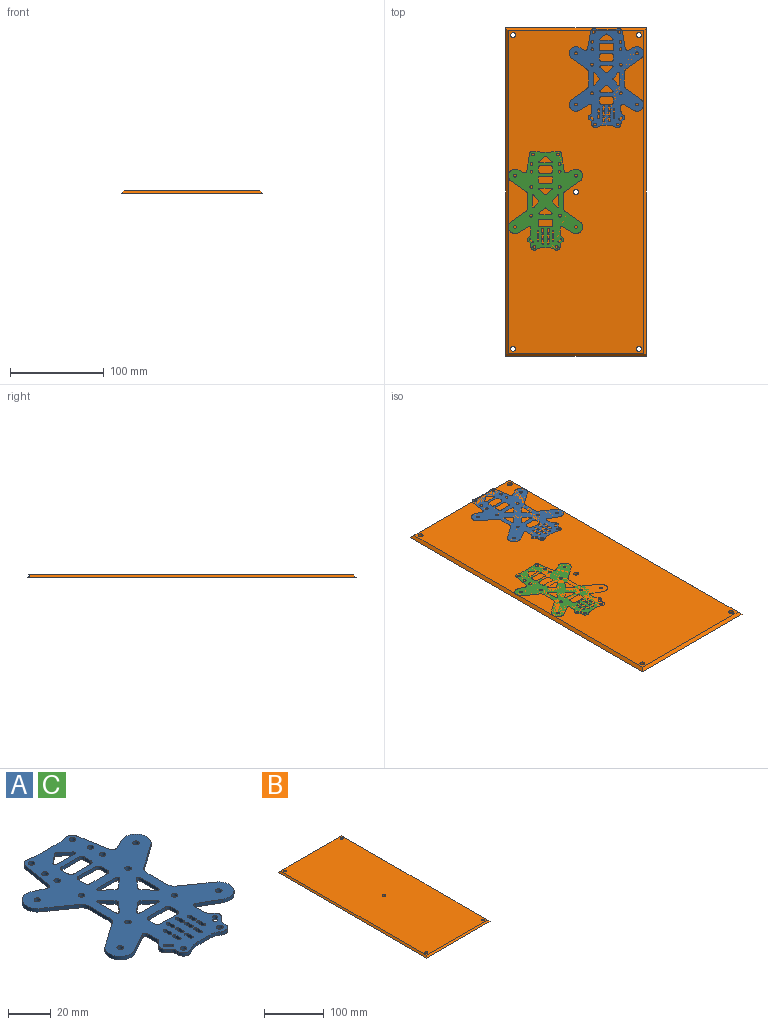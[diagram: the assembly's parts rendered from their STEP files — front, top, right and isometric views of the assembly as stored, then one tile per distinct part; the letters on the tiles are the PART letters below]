
ASSEMBLY  parts=3 mates=2
PART A: 170 faces, bbox 79.1x105.5x2 mm
  f0: plane 2.12x2.12mm, normal (0.71,0.71,0), area 6mm2, adj f1,f134,f168,f169
  f1: cylinder r=1mm len=2mm, axis (0,0,-1), area 6.3mm2, adj f0,f2,f168,f169
  f2: plane 2.12x2.12mm, normal (-0.71,-0.71,0), area 6mm2, adj f1,f134,f168,f169
  f3: cylinder r=1mm len=2mm, axis (0,0,-1), area 6.3mm2, adj f4,f135,f168,f169
  f4: plane 3x2mm, normal (1,0,0), area 6mm2, adj f3,f5,f168,f169
  f5: cylinder r=1mm len=2mm, axis (0,0,-1), area 6.3mm2, adj f4,f135,f168,f169
  f6: plane 3x2mm, normal (1,0,0), area 6mm2, adj f7,f136,f168,f169
  f7: cylinder r=1mm len=2mm, axis (0,0,-1), area 6.3mm2, adj f6,f8,f168,f169
  f8: plane 3x2mm, normal (-1,0,0), area 6mm2, adj f7,f136,f168,f169
  f9: plane 3x2mm, normal (1,0,0), area 6mm2, adj f10,f137,f168,f169
  f10: cylinder r=1mm len=2mm, axis (0,0,-1), area 6.3mm2, adj f9,f11,f168,f169
  f11: plane 3x2mm, normal (-1,0,0), area 6mm2, adj f10,f137,f168,f169
  f12: plane 3x2mm, normal (1,0,0), area 6mm2, adj f13,f138,f168,f169
  f13: cylinder r=1mm len=2mm, axis (0,0,-1), area 6.3mm2, adj f12,f14,f168,f169
  f14: plane 3x2mm, normal (-1,0,0), area 6mm2, adj f13,f138,f168,f169
  f15: plane 3x2mm, normal (1,0,0), area 6mm2, adj f16,f139,f168,f169
  f16: cylinder r=1mm len=2mm, axis (0,0,-1), area 6.3mm2, adj f15,f17,f168,f169
  f17: plane 3x2mm, normal (-1,0,0), area 6mm2, adj f16,f139,f168,f169
  f18: cylinder r=3.5mm len=5.53mm, axis (0,0,-1), area 15.3mm2, adj f19,f140,f168,f169
  f19: plane 2x1.24mm, normal (1,0,0), area 2.5mm2, adj f18,f20,f168,f169
  f20: cylinder r=3mm len=2.12mm, axis (0,0,-1), area 4.7mm2, adj f19,f21,f168,f169
  f21: plane 2.12x2.12mm, normal (0.71,-0.71,0), area 6mm2, adj f20,f22,f168,f169
  f22: cylinder r=3mm len=4.24mm, axis (0,0,-1), area 9.4mm2, adj f21,f23,f168,f169
  f23: plane 2.41x2.41mm, normal (0.71,0.71,0), area 6.8mm2, adj f22,f24,f168,f169
  f24: cylinder r=2mm len=2mm, axis (0,0,-1), area 3.1mm2, adj f23,f25,f168,f169
  f25: plane 6.65x2mm, normal (1,0,0), area 13.3mm2, adj f24,f26,f168,f169
  f26: cylinder r=1.5mm len=2.25mm, axis (0,0,-1), area 6.3mm2, adj f25,f27,f168,f169
  f27: plane 11.16x6.44mm, normal (-0.5,-0.87,0), area 25.8mm2, adj f26,f28,f168,f169
  f28: cylinder r=7.09mm len=12.9mm, axis (0,0,-1), area 43.3mm2, adj f27,f29,f168,f169
  f29: plane 15.33x10.73mm, normal (0.57,0.82,0), area 37.4mm2, adj f28,f30,f168,f169
  f30: cylinder r=5.14mm len=4.21mm, axis (0,0,-1), area 9.9mm2, adj f29,f31,f168,f169
  f31: plane 13.09x2mm, normal (1,0,0), area 26.2mm2, adj f30,f32,f168,f169
  f32: cylinder r=5.14mm len=4.21mm, axis (0,0,-1), area 9.9mm2, adj f31,f33,f168,f169
  f33: plane 15.33x10.73mm, normal (0.57,-0.82,0), area 37.4mm2, adj f32,f34,f168,f169
  f34: cylinder r=7.09mm len=12.9mm, axis (0,0,-1), area 42.4mm2, adj f33,f35,f168,f169
  f35: plane 6.13x3.03mm, normal (-0.44,0.9,0), area 13.7mm2, adj f34,f36,f168,f169
  f36: cylinder r=2.22mm len=3.18mm, axis (0,0,-1), area 8.3mm2, adj f35,f37,f168,f169
  f37: plane 18.33x3.05mm, normal (0.99,0.16,0), area 37.2mm2, adj f36,f38,f168,f169
  f38: cylinder r=3.5mm len=3.97mm, axis (0,0,-1), area 10.9mm2, adj f37,f39,f168,f169
  f39: plane 4.22x2mm, normal (-0.15,0.99,0), area 8.5mm2, adj f38,f40,f168,f169
  f40: cylinder r=24.09mm len=3.54mm, axis (0,0,-1), area 7.1mm2, adj f39,f41,f168,f169
  f41: plane 10.45x2mm, normal (0,1,0), area 20.9mm2, adj f40,f42,f168,f169
  f42: cylinder r=24.09mm len=3.54mm, axis (0,0,-1), area 7.1mm2, adj f41,f43,f168,f169
  f43: plane 4.22x2mm, normal (0.15,0.99,0), area 8.5mm2, adj f42,f44,f168,f169
  f44: cylinder r=3.5mm len=3.97mm, axis (0,0,-1), area 10.9mm2, adj f43,f45,f168,f169
  f45: plane 18.33x3.05mm, normal (-0.99,0.16,0), area 37.2mm2, adj f44,f46,f168,f169
  f46: cylinder r=2.22mm len=3.18mm, axis (0,0,-1), area 8.3mm2, adj f45,f47,f168,f169
  f47: plane 6.13x3.03mm, normal (0.44,0.9,0), area 13.7mm2, adj f46,f48,f168,f169
  f48: cylinder r=7.09mm len=12.9mm, axis (0,0,-1), area 42.4mm2, adj f47,f49,f168,f169
  f49: plane 15.33x10.73mm, normal (-0.57,-0.82,0), area 37.4mm2, adj f48,f50,f168,f169
  f50: cylinder r=5.14mm len=4.21mm, axis (0,0,-1), area 9.9mm2, adj f49,f51,f168,f169
  f51: plane 13.09x2mm, normal (-1,0,0), area 26.2mm2, adj f50,f52,f168,f169
  f52: cylinder r=5.14mm len=4.21mm, axis (0,0,-1), area 9.9mm2, adj f51,f53,f168,f169
  f53: plane 15.33x10.73mm, normal (-0.57,0.82,0), area 37.4mm2, adj f52,f54,f168,f169
  f54: cylinder r=7.09mm len=12.9mm, axis (0,0,-1), area 43.3mm2, adj f53,f55,f168,f169
  f55: plane 11.16x6.44mm, normal (0.5,-0.87,0), area 25.8mm2, adj f54,f56,f168,f169
  f56: cylinder r=1.5mm len=2.25mm, axis (0,0,-1), area 6.3mm2, adj f55,f57,f168,f169
  f57: plane 6.65x2mm, normal (-1,0,0), area 13.3mm2, adj f56,f58,f168,f169
  f58: cylinder r=2mm len=2mm, axis (0,0,-1), area 3.1mm2, adj f57,f59,f168,f169
  f59: plane 2.41x2.41mm, normal (-0.71,0.71,0), area 6.8mm2, adj f58,f60,f168,f169
  f60: cylinder r=3mm len=4.24mm, axis (0,0,-1), area 9.4mm2, adj f59,f61,f168,f169
  f61: plane 2.12x2.12mm, normal (-0.71,-0.71,0), area 6mm2, adj f60,f62,f168,f169
  f62: cylinder r=3mm len=2.12mm, axis (0,0,-1), area 4.7mm2, adj f61,f63,f168,f169
  f63: plane 2x1.24mm, normal (-1,0,0), area 2.5mm2, adj f62,f64,f168,f169
  f64: cylinder r=3.5mm len=5.53mm, axis (0,0,-1), area 15.3mm2, adj f63,f65,f168,f169
  f65: cylinder r=10mm len=5.8mm, axis (0,0,-1), area 12.4mm2, adj f64,f66,f168,f169
  f66: plane 8.35x2mm, normal (0,-1,0), area 16.7mm2, adj f65,f140,f168,f169
  f67: plane 11x2mm, normal (0,1,0), area 22mm2, adj f68,f141,f168,f169
  f68: cylinder r=2mm len=2mm, axis (0,0,-1), area 6.3mm2, adj f67,f69,f168,f169
  f69: plane 4x2mm, normal (1,0,0), area 8mm2, adj f68,f70,f168,f169
  f70: cylinder r=2mm len=2mm, axis (0,0,-1), area 6.3mm2, adj f69,f71,f168,f169
  f71: plane 11x2mm, normal (0,-1,0), area 22mm2, adj f70,f72,f168,f169
  f72: cylinder r=2mm len=2mm, axis (0,0,-1), area 6.3mm2, adj f71,f73,f168,f169
  f73: plane 4x2mm, normal (-1,0,0), area 8mm2, adj f72,f141,f168,f169
  f74: plane 11x2mm, normal (0,1,0), area 22mm2, adj f75,f142,f168,f169
  f75: cylinder r=2mm len=2mm, axis (0,0,-1), area 6.3mm2, adj f74,f76,f168,f169
  f76: plane 4x2mm, normal (1,0,0), area 8mm2, adj f75,f77,f168,f169
  f77: cylinder r=2mm len=2mm, axis (0,0,-1), area 6.3mm2, adj f76,f78,f168,f169
  f78: plane 11x2mm, normal (0,-1,0), area 22mm2, adj f77,f79,f168,f169
  f79: cylinder r=2mm len=2mm, axis (0,0,-1), area 6.3mm2, adj f78,f80,f168,f169
  f80: plane 4x2mm, normal (-1,0,0), area 8mm2, adj f79,f142,f168,f169
  f81: cylinder r=1mm len=2mm, axis (0,0,-1), area 2.8mm2, adj f82,f143,f168,f169
  f82: plane 6x5.03mm, normal (-0.77,0.64,0), area 15.7mm2, adj f81,f83,f168,f169
  f83: cylinder r=1mm len=2mm, axis (0,0,-1), area 4.9mm2, adj f82,f84,f168,f169
  f84: plane 12x2mm, normal (1,0,0), area 24mm2, adj f83,f85,f168,f169
  f85: cylinder r=1mm len=2mm, axis (0,0,-1), area 4.9mm2, adj f84,f143,f168,f169
  f86: plane 6x5.03mm, normal (-0.64,-0.77,0), area 15.7mm2, adj f87,f144,f168,f169
  f87: cylinder r=1mm len=2mm, axis (0,0,-1), area 4.9mm2, adj f86,f88,f168,f169
  f88: plane 12x2mm, normal (0,1,0), area 24mm2, adj f87,f89,f168,f169
  f89: cylinder r=1mm len=2mm, axis (0,0,-1), area 4.9mm2, adj f88,f90,f168,f169
  f90: plane 6x5.03mm, normal (0.64,-0.77,0), area 15.7mm2, adj f89,f144,f168,f169
  f91: plane 6x5.03mm, normal (0.77,-0.64,0), area 15.7mm2, adj f92,f145,f168,f169
  f92: cylinder r=1mm len=2mm, axis (0,0,-1), area 4.9mm2, adj f91,f93,f168,f169
  f93: plane 12x2mm, normal (-1,0,0), area 24mm2, adj f92,f94,f168,f169
  f94: cylinder r=1mm len=2mm, axis (0,0,-1), area 4.9mm2, adj f93,f95,f168,f169
  f95: plane 6x5.03mm, normal (0.77,0.64,0), area 15.7mm2, adj f94,f145,f168,f169
  f96: plane 6x5.03mm, normal (0.64,0.77,0), area 15.7mm2, adj f97,f146,f168,f169
  f97: cylinder r=1mm len=2mm, axis (0,0,-1), area 4.9mm2, adj f96,f98,f168,f169
  f98: plane 12x2mm, normal (0,-1,0), area 24mm2, adj f97,f99,f168,f169
  f99: cylinder r=1mm len=2mm, axis (0,0,-1), area 4.9mm2, adj f98,f100,f168,f169
  f100: plane 6x5.03mm, normal (-0.64,0.77,0), area 15.7mm2, adj f99,f146,f168,f169
  f101: cylinder r=1mm len=2mm, axis (0,0,-1), area 4.9mm2, adj f102,f147,f168,f169
  f102: plane 12x2mm, normal (0,1,0), area 24mm2, adj f101,f103,f168,f169
  f103: cylinder r=1mm len=2mm, axis (0,0,-1), area 4.9mm2, adj f102,f104,f168,f169
  f104: plane 6x5.03mm, normal (0.64,-0.77,0), area 15.7mm2, adj f103,f105,f168,f169
  f105: cylinder r=1mm len=2mm, axis (0,0,-1), area 2.8mm2, adj f104,f147,f168,f169
  f106: cylinder r=1mm len=2mm, axis (0,0,-1), area 6.3mm2, adj f107,f148,f168,f169
  f107: plane 3x2mm, normal (-1,0,0), area 6mm2, adj f106,f108,f168,f169
  f108: cylinder r=1mm len=2mm, axis (0,0,-1), area 6.3mm2, adj f107,f148,f168,f169
  f109: plane 3x2mm, normal (-1,0,0), area 6mm2, adj f110,f149,f168,f169
  f110: cylinder r=1mm len=2mm, axis (0,0,-1), area 6.3mm2, adj f109,f111,f168,f169
  f111: plane 3x2mm, normal (1,0,0), area 6mm2, adj f110,f149,f168,f169
  f112: cylinder r=1mm len=2mm, axis (0,0,-1), area 6.3mm2, adj f113,f150,f168,f169
  f113: plane 3x2mm, normal (1,0,0), area 6mm2, adj f112,f114,f168,f169
  f114: cylinder r=1mm len=2mm, axis (0,0,-1), area 6.3mm2, adj f113,f150,f168,f169
  f115: plane 11x2mm, normal (0,1,0), area 22mm2, adj f116,f151,f168,f169
  f116: cylinder r=2mm len=2mm, axis (0,0,-1), area 6.3mm2, adj f115,f117,f168,f169
  f117: plane 4x2mm, normal (1,0,0), area 8mm2, adj f116,f118,f168,f169
  f118: cylinder r=2mm len=2mm, axis (0,0,-1), area 6.3mm2, adj f117,f119,f168,f169
  f119: plane 11x2mm, normal (0,-1,0), area 22mm2, adj f118,f120,f168,f169
  f120: cylinder r=2mm len=2mm, axis (0,0,-1), area 6.3mm2, adj f119,f121,f168,f169
  f121: plane 4x2mm, normal (-1,0,0), area 8mm2, adj f120,f151,f168,f169
  f122: plane 3x2mm, normal (-1,0,0), area 6mm2, adj f123,f152,f168,f169
  f123: cylinder r=1mm len=2mm, axis (0,0,-1), area 6.3mm2, adj f122,f124,f168,f169
  f124: plane 3x2mm, normal (1,0,0), area 6mm2, adj f123,f152,f168,f169
  f125: cylinder r=1mm len=2mm, axis (0,0,-1), area 6.3mm2, adj f126,f153,f168,f169
  f126: plane 3x2mm, normal (1,0,0), area 6mm2, adj f125,f127,f168,f169
  f127: cylinder r=1mm len=2mm, axis (0,0,-1), area 6.3mm2, adj f126,f153,f168,f169
  f128: plane 2.12x2.12mm, normal (-0.71,0.71,0), area 6mm2, adj f129,f154,f168,f169
  f129: cylinder r=1mm len=2mm, axis (0,0,-1), area 6.3mm2, adj f128,f130,f168,f169
  f130: plane 2.12x2.12mm, normal (0.71,-0.71,0), area 6mm2, adj f129,f154,f168,f169
  f131: cylinder r=1.5mm len=3mm, axis (0,0,-1), area 18.8mm2, adj f168,f169
  f132: cylinder r=1.5mm len=3mm, axis (0,0,-1), area 18.8mm2, adj f168,f169
  f133: cylinder r=1.5mm len=3mm, axis (0,0,-1), area 18.8mm2, adj f168,f169
  f134: cylinder r=1mm len=2mm, axis (0,0,-1), area 6.3mm2, adj f0,f2,f168,f169
  f135: plane 3x2mm, normal (-1,0,0), area 6mm2, adj f3,f5,f168,f169
  f136: cylinder r=1mm len=2mm, axis (0,0,-1), area 6.3mm2, adj f6,f8,f168,f169
  f137: cylinder r=1mm len=2mm, axis (0,0,-1), area 6.3mm2, adj f9,f11,f168,f169
  f138: cylinder r=1mm len=2mm, axis (0,0,-1), area 6.3mm2, adj f12,f14,f168,f169
  f139: cylinder r=1mm len=2mm, axis (0,0,-1), area 6.3mm2, adj f15,f17,f168,f169
  f140: cylinder r=10mm len=5.8mm, axis (0,0,-1), area 12.4mm2, adj f18,f66,f168,f169
  f141: cylinder r=2mm len=2mm, axis (0,0,-1), area 6.3mm2, adj f67,f73,f168,f169
  f142: cylinder r=2mm len=2mm, axis (0,0,-1), area 6.3mm2, adj f74,f80,f168,f169
  f143: plane 6x5.03mm, normal (-0.77,-0.64,0), area 15.7mm2, adj f81,f85,f168,f169
  f144: cylinder r=1mm len=2mm, axis (0,0,-1), area 2.8mm2, adj f86,f90,f168,f169
  f145: cylinder r=1mm len=2mm, axis (0,0,-1), area 2.8mm2, adj f91,f95,f168,f169
  f146: cylinder r=1mm len=2mm, axis (0,0,-1), area 2.8mm2, adj f96,f100,f168,f169
  f147: plane 6x5.03mm, normal (-0.64,-0.77,0), area 15.7mm2, adj f101,f105,f168,f169
  f148: plane 3x2mm, normal (1,0,0), area 6mm2, adj f106,f108,f168,f169
  f149: cylinder r=1mm len=2mm, axis (0,0,-1), area 6.3mm2, adj f109,f111,f168,f169
  f150: plane 3x2mm, normal (-1,0,0), area 6mm2, adj f112,f114,f168,f169
  f151: cylinder r=2mm len=2mm, axis (0,0,-1), area 6.3mm2, adj f115,f121,f168,f169
  f152: cylinder r=1mm len=2mm, axis (0,0,-1), area 6.3mm2, adj f122,f124,f168,f169
  f153: plane 3x2mm, normal (-1,0,0), area 6mm2, adj f125,f127,f168,f169
  f154: cylinder r=1mm len=2mm, axis (0,0,-1), area 6.3mm2, adj f128,f130,f168,f169
  f155: cylinder r=1.5mm len=3mm, axis (0,0,-1), area 18.8mm2, adj f168,f169
  f156: cylinder r=1.5mm len=3mm, axis (0,0,-1), area 18.8mm2, adj f168,f169
  f157: cylinder r=1.5mm len=3mm, axis (0,0,-1), area 18.8mm2, adj f168,f169
  f158: cylinder r=1.5mm len=3mm, axis (0,0,-1), area 18.8mm2, adj f168,f169
  f159: cylinder r=1.5mm len=3mm, axis (0,0,-1), area 18.8mm2, adj f168,f169
  f160: cylinder r=1.5mm len=3mm, axis (0,0,-1), area 18.8mm2, adj f168,f169
  f161: cylinder r=1.5mm len=3mm, axis (0,0,-1), area 18.8mm2, adj f168,f169
  f162: cylinder r=1.5mm len=3mm, axis (0,0,-1), area 18.8mm2, adj f168,f169
  f163: cylinder r=1.5mm len=3mm, axis (0,0,-1), area 18.8mm2, adj f168,f169
  f164: cylinder r=1.5mm len=3mm, axis (0,0,-1), area 18.8mm2, adj f168,f169
  f165: cylinder r=1.5mm len=3mm, axis (0,0,-1), area 18.8mm2, adj f168,f169
  f166: cylinder r=1.5mm len=3mm, axis (0,0,-1), area 18.8mm2, adj f168,f169
  f167: cylinder r=1.5mm len=3mm, axis (0,0,-1), area 18.8mm2, adj f168,f169
  f168: plane 105.5x79.08mm, normal (0,0,1), area 4198.1mm2, adj f0,f1,f2,f3,f4,f5,f6,f7
  f169: plane 105.5x79.08mm, normal (0,0,-1), area 4198.1mm2, adj f0,f1,f2,f3,f4,f5,f6,f7
PART B: 11 faces, bbox 150x350x3 mm
  f0: plane 344x144mm, normal (0,0,1), area 49429.8mm2, adj f2,f3,f4,f5,f6,f7,f8,f9
  f1: plane 350x150mm, normal (0,0,-1), area 52393.8mm2, adj f2,f3,f4,f5,f6,f7,f8,f9
  f2: cylinder r=2.6mm len=5.2mm, axis (0,0,-1), area 49mm2, adj f0,f1
  f3: cylinder r=2.6mm len=5.2mm, axis (0,0,-1), area 49mm2, adj f0,f1
  f4: cylinder r=2.6mm len=5.2mm, axis (0,0,-1), area 49mm2, adj f0,f1
  f5: cylinder r=2.6mm len=5.2mm, axis (0,0,-1), area 49mm2, adj f0,f1
  f6: cylinder r=2.6mm len=5.2mm, axis (0,0,-1), area 49mm2, adj f0,f1
  f7: plane 150x3mm, normal (0,0.71,0.71), area 623.7mm2, adj f0,f1,f8,f9
  f8: plane 350x3mm, normal (0.71,0,0.71), area 1472.2mm2, adj f0,f1,f7,f10
  f9: plane 350x3mm, normal (-0.71,0,0.71), area 1472.2mm2, adj f0,f1,f7,f10
  f10: plane 150x3mm, normal (0,-0.71,0.71), area 623.7mm2, adj f0,f1,f8,f9
PART C: same geometry as A
PLACE A t=(32.42,120.37,1)mm
PLACE B at identity fixed
PLACE C t=(-32.47,-9.98,1)mm
MATE planar C.f168 <-> B.f2  axis (0,0,1) through (-32.47,-8.87,3)mm
MATE planar A.f168 <-> B.f2  axis (0,0,1) through (32.42,121.49,3)mm
